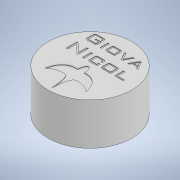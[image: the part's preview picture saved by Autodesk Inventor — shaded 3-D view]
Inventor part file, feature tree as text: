
AUTODESK INVENTOR PART (.ipt)
format: ipt  version: 2021 (Build 250183000, 183)  size: 313,344 bytes
history: native  units: in
note: dims shown in document units (in); Inventor stores cm internally (conversion verified against a paired STEP export)
features: other x2, extrude x1, sketch x1
ambient origin geometry x8: Origin, YZ Plane, XZ Plane, XY Plane, X Axis, Y Axis, Z Axis, Center Point
bodies: Solid1 (feature_tree)
feature tree (4):
  other  "Pastel.stp"
  extrude  "Extrusion1"  [1 undecoded]
  sketch  "Sketch1"  dims[d0=0.3937in d1=0.0in]
  other  "Sólido1"
note: 1 required parameter value undecoded (feature->parameter linkage not recoverable at this tier; creation-order binding heuristic only, values carry confidence <= 0.55)
